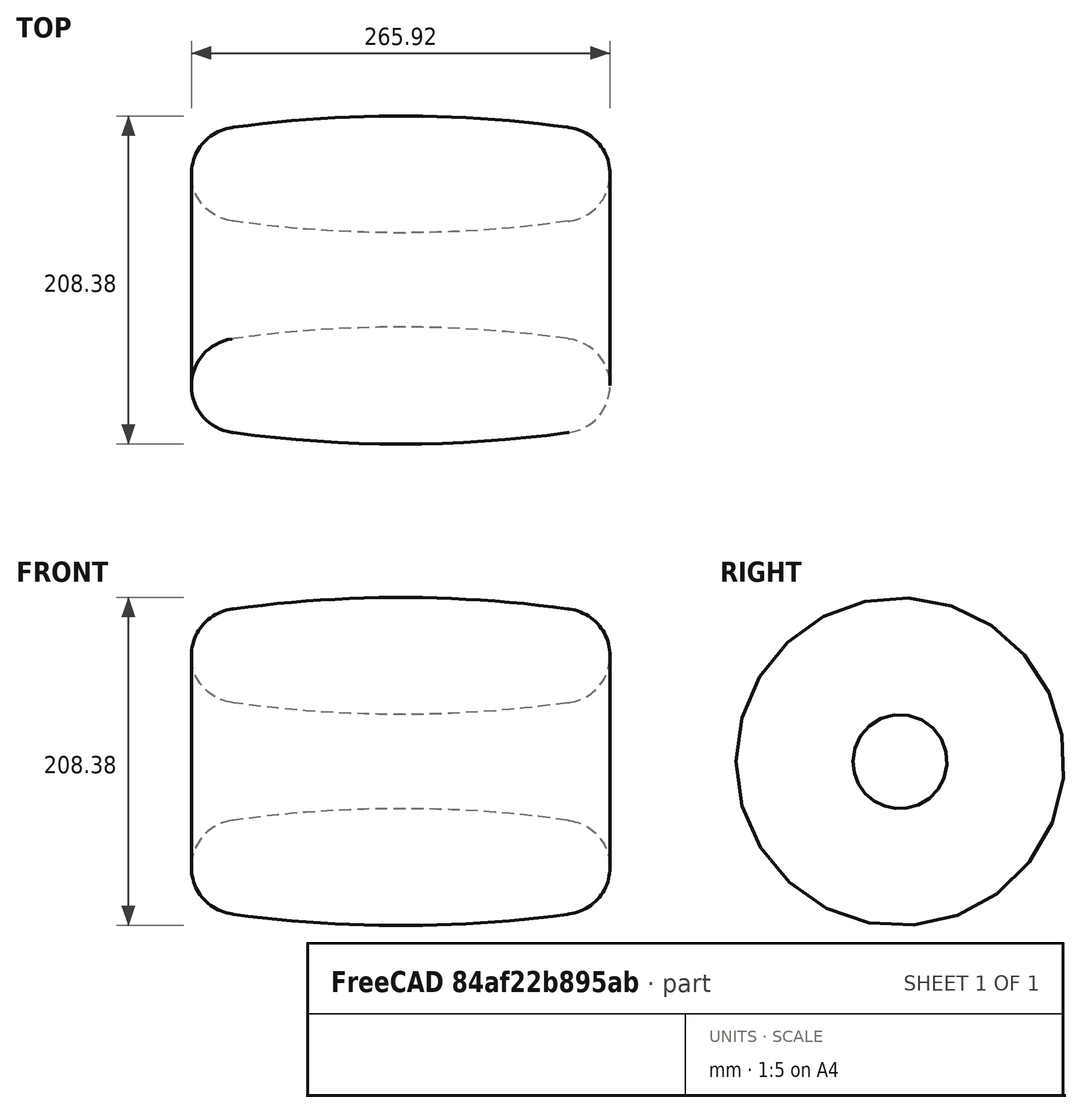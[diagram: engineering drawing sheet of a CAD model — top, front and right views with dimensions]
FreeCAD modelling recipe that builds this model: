
FCSTD DOCUMENT
Label: pr_004
objects: Sketcher::SketchObject×1, PartDesign::Revolution×1
note: 2 computed .brp shape members not serialized (recipe doc carries the construction recipe); baked Part::Feature solids carry a one-line shape summary decoded from their .brp

FEATURE [Sketcher::SketchObject] Sketch
  sketch-geometry (8):
    g0: ArcOfCircle CenterX=0 CenterY=-796.929 CenterZ=0 NormalX=0 NormalY=0 NormalZ=1 Radius=767 StartAngle=1.432 EndAngle=1.70959
    g1: ArcOfCircle CenterX=0 CenterY=682.812 CenterZ=0 NormalX=0 NormalY=0 NormalZ=1 Radius=787 StartAngle=4.57728 EndAngle=4.8475
    g2: ArcOfCircle CenterX=-102.956 CenterY=-67.1549 CenterZ=0 NormalX=0 NormalY=0 NormalZ=1 Radius=30 StartAngle=1.70959 EndAngle=4.57728
    g3: ArcOfCircle CenterX=102.956 CenterY=-67.1549 CenterZ=0 NormalX=0 NormalY=0 NormalZ=1 Radius=30 StartAngle=4.8475 EndAngle=7.71518
    g4: LineSegment StartX=106.116 StartY=-37.3051 StartZ=0 EndX=107.107 EndY=-37.4434 EndZ=0
    g5: LineSegment StartX=-107.107 StartY=-37.4434 StartZ=0 EndX=-106.116 EndY=-37.3051 EndZ=0
    g6: LineSegment StartX=-106.997 StartY=-96.8815 StartZ=0 EndX=-106.006 EndY=-97.0162 EndZ=0
    g7: LineSegment StartX=106.006 StartY=-97.0162 StartZ=0 EndX=106.997 EndY=-96.8815 EndZ=0
  constraints (18):
    c: Radius(g0) = 767
    c: Radius(g1) = 787
    c: Radius(g2) = 30
    c: Radius(g3) = 30
    c: Tangent(g0,g4)
    c: Tangent(g3,g4)
    c: Tangent(g2,g5)
    c: Tangent(g5,g0)
    c: Tangent(g2,g6)
    c: Tangent(g6,g1)
    c: Tangent(g1,g7)
    c: Tangent(g7,g3)
    c: Distance(g5) = 1
    c: Distance(g6) = 1
    c: DistanceX(g0) = 0
    c: DistanceX(g1) = 0
    c: Distance(g4) = 1
    c: Distance(g7) = 1
FEATURE [PartDesign::Revolution] Revolution
  Angle = 360
  Axis = (1,0,0)
  Base = (0,0,0)
  Sketch = -> Sketch
